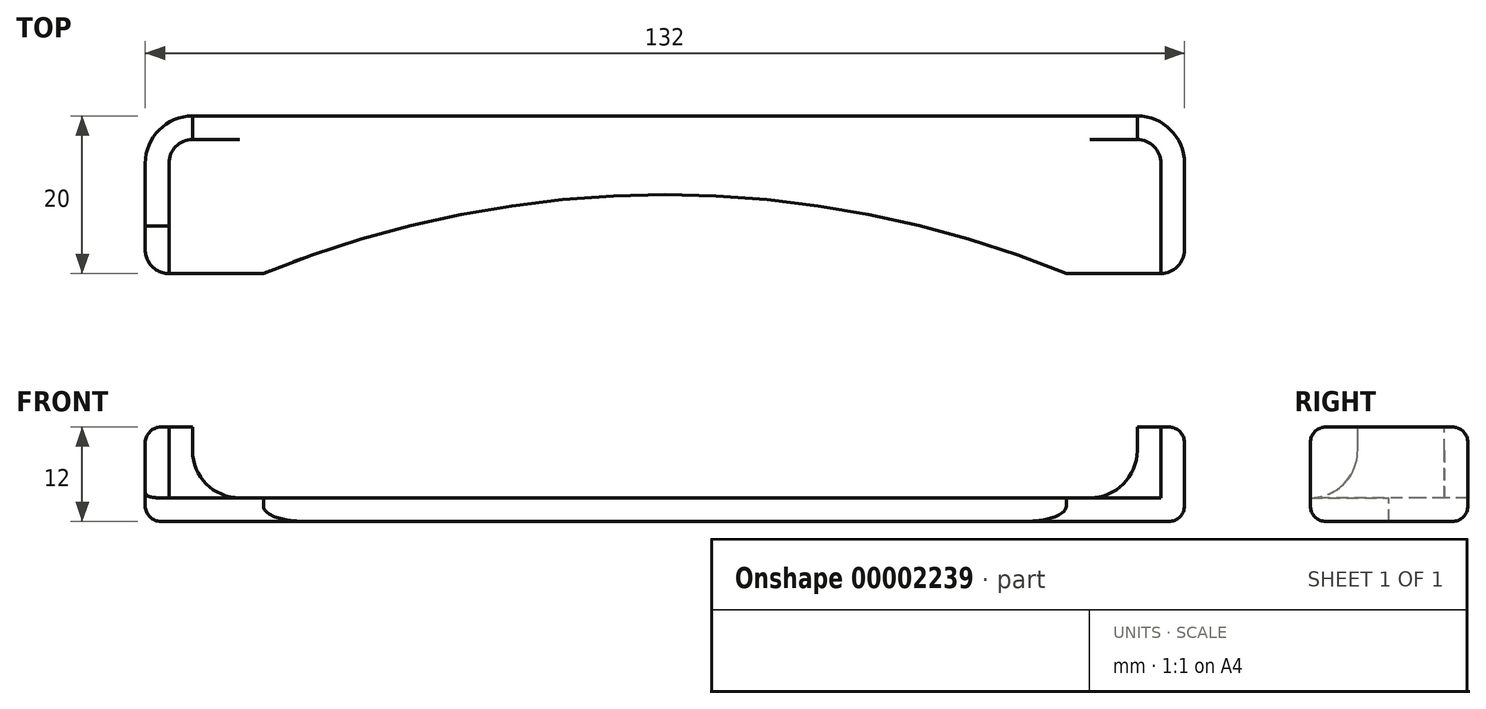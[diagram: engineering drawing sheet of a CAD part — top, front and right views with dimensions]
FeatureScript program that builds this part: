
annotation { "Feature Type Name" : "Feature", "Feature Type Description" : "" }
export const myFeature = defineFeature(function(context is Context, id is Id, definition is map)
    precondition{}
    {
        {
            var Q0;
            Q0=qCreatedBy(makeId("Top.planeOp"),FACE);
            var sketch = newSketch(context, id + "F0", { "sketchPlane" : qUnion([Q0])});
            skLineSegment(sketch, "E0.bottom", {"start": v(-60, 35) * mm, "end": v(60, 35) * mm});
            skLineSegment(sketch, "E0.top", {"start": v(-63, 15) * mm, "end": v(63, 15) * mm});
            skLineSegment(sketch, "E0.left", {"start": v(-66, 29) * mm, "end": v(-66, 18) * mm});
            skLineSegment(sketch, "E0.right", {"start": v(66, 29) * mm, "end": v(66, 18) * mm});
            skPoint(sketch, "E1.visualSharp", {"position": v(-66, 35) * mm});
            skArc(sketch, "E1.filletArc", {"start": v(-60, 35) * mm, "mid": v(-64.24, 33.24) * mm, "end": v(-66, 29) * mm});
            skPoint(sketch, "E2.visualSharp", {"position": v(66, 35) * mm});
            skArc(sketch, "E2.filletArc", {"start": v(66, 29) * mm, "mid": v(64.24, 33.24) * mm, "end": v(60, 35) * mm});
            skPoint(sketch, "E3.visualSharp", {"position": v(-66, 15) * mm});
            skArc(sketch, "E3.filletArc", {"start": v(-66, 18) * mm, "mid": v(-65.12, 15.88) * mm, "end": v(-63, 15) * mm});
            skPoint(sketch, "E4.visualSharp", {"position": v(66, 15) * mm});
            skArc(sketch, "E4.filletArc", {"start": v(63, 15) * mm, "mid": v(65.12, 15.88) * mm, "end": v(66, 18) * mm});
            skPoint(sketch, "E5", {"position": v(0, 15) * mm});
            skSolve(sketch);
        }
        {
            var Q0;
            Q0=makeQuery(id+"F0.imprint","IMPRINT",FACE,{"disambiguationData":[TD([[makeQuery(id+"F0.imprint","IMPRINT",EDGE,{"derivedFrom":sQuery(id+"F0.wireOp",EDGE,"E0.bottom")}),-1.0]])]});
            extrude(context, id + "F1", {"entities" : qUnion([Q0]), "depth" : 12 * mm});
        }
        {
            var Q0;
            Q0=makeQuery(id+"F1.opExtrude","CAP_FACE",FACE,{"disambiguationData":[OSD([sQuery(id+"F0.wireOp",EDGE,"E0.bottom"),sQuery(id+"F0.wireOp",EDGE,"E0.top"),sQuery(id+"F0.wireOp",EDGE,"E0.left"),sQuery(id+"F0.wireOp",EDGE,"E0.right"),sQuery(id+"F0.wireOp",EDGE,"E1.filletArc"),sQuery(id+"F0.wireOp",EDGE,"E2.filletArc"),sQuery(id+"F0.wireOp",EDGE,"E3.filletArc"),sQuery(id+"F0.wireOp",EDGE,"E4.filletArc")])],"isStart":false});
            var sketch = newSketch(context, id + "F2", { "sketchPlane" : qUnion([Q0])});
            skArc(sketch, "E6.1", {"start": v(63, 29) * mm, "mid": v(62.12, 31.12) * mm, "end": v(60, 32) * mm});
            skLineSegment(sketch, "E6.2", {"start": v(-60, 32) * mm, "end": v(60, 32) * mm});
            skArc(sketch, "E6.3", {"start": v(-60, 32) * mm, "mid": v(-62.12, 31.12) * mm, "end": v(-63, 29) * mm});
            skLineSegment(sketch, "E7", {"start": v(-63, 29) * mm, "end": v(-63, 15) * mm});
            skLineSegment(sketch, "E8", {"start": v(-63, 15) * mm, "end": v(63, 15) * mm});
            skLineSegment(sketch, "E9", {"start": v(63, 15) * mm, "end": v(63, 29) * mm});
            skSolve(sketch);
        }
        {
            var Q0;
            Q0=makeQuery(id+"F1.opExtrude","CAP_FACE",FACE,{"disambiguationData":[OSD([sQuery(id+"F0.wireOp",EDGE,"E0.bottom"),sQuery(id+"F0.wireOp",EDGE,"E0.top"),sQuery(id+"F0.wireOp",EDGE,"E0.left"),sQuery(id+"F0.wireOp",EDGE,"E0.right"),sQuery(id+"F0.wireOp",EDGE,"E1.filletArc"),sQuery(id+"F0.wireOp",EDGE,"E2.filletArc"),sQuery(id+"F0.wireOp",EDGE,"E3.filletArc"),sQuery(id+"F0.wireOp",EDGE,"E4.filletArc")])],"isStart":false});
            var Q1;
            Q1=makeQuery(id+"F1.opExtrude","CAP_FACE",FACE,{"disambiguationData":[OSD([sQuery(id+"F0.wireOp",EDGE,"E0.bottom"),sQuery(id+"F0.wireOp",EDGE,"E0.top"),sQuery(id+"F0.wireOp",EDGE,"E0.left"),sQuery(id+"F0.wireOp",EDGE,"E0.right"),sQuery(id+"F0.wireOp",EDGE,"E1.filletArc"),sQuery(id+"F0.wireOp",EDGE,"E2.filletArc"),sQuery(id+"F0.wireOp",EDGE,"E3.filletArc"),sQuery(id+"F0.wireOp",EDGE,"E4.filletArc")])],"isStart":true});
            fillet(context, id + "F3", {"entities" : qUnion([Q0, Q1]), "radius" : 2 * mm, "allowEdgeOverflow" : false});
        }
        {
            var Q0;
            Q0=makeQuery(id+"F2.imprint","IMPRINT",FACE,{"disambiguationData":[TD([[makeQuery(id+"F2.imprint","IMPRINT",EDGE,{"derivedFrom":sQuery(id+"F2.wireOp",EDGE,"001a4620-0fa9-427e-a59e-a394cfe2f85a.bottom")}),-1.0]])]});
            var Q1;
            Q1=makeQuery(id+"F2.imprint","IMPRINT",FACE,{"disambiguationData":[TD([[makeQuery(id+"F2.imprint","IMPRINT",EDGE,{"derivedFrom":sQuery(id+"F2.wireOp",EDGE,"E6.1")}),1.0]])]});
            extrude(context, id + "F4", {"entities" : qUnion([Q0, Q1]), "operationType" : NewBodyOperationType.REMOVE, "oppositeDirection" : true, "depth" : 9 * mm});
        }
        {
            var Q0;
            Q0=makeQuery(id+"F4.boolean.opBoolean","COPY",FACE,{"derivedFrom":makeQuery(id+"F4.opExtrude","CAP_FACE",FACE,{"disambiguationData":[OSD([sQuery(id+"F2.wireOp",EDGE,"E6.1"),sQuery(id+"F2.wireOp",EDGE,"E6.2"),sQuery(id+"F2.wireOp",EDGE,"E6.3"),sQuery(id+"F2.wireOp",EDGE,"E7"),sQuery(id+"F2.wireOp",EDGE,"E8"),sQuery(id+"F2.wireOp",EDGE,"E9")])],"isStart":false})});
            var sketch = newSketch(context, id + "F5", { "sketchPlane" : qUnion([Q0])});
            skArc(sketch, "E10", {"start": v(51, 15) * mm, "mid": v(0, 25) * mm, "end": v(-51, 15) * mm});
            skLineSegment(sketch, "E11", {"start": v(-51, 15) * mm, "end": v(51, 15) * mm});
            skLineSegment(sketch, "E12", {"start": v(0, 15) * mm, "end": v(0, -110.05) * mm, "construction": true});
            skSolve(sketch);
        }
        {
            var Q0;
            Q0=makeQuery(id+"F5.imprint","IMPRINT",FACE,{"disambiguationData":[TD([[makeQuery(id+"F5.imprint","IMPRINT",EDGE,{"derivedFrom":sQuery(id+"F5.wireOp",EDGE,"E10")}),1.0]])]});
            extrude(context, id + "F6", {"entities" : qUnion([Q0]), "operationType" : NewBodyOperationType.REMOVE, "endBound" : BoundingType.THROUGH_ALL, "oppositeDirection" : true, "depth" : 25 * mm});
        }
        {
            var Q0;
            Q0=makeQuery(id+"F4.boolean.opBoolean","COPY",FACE,{"derivedFrom":makeQuery(id+"F4.opExtrude","SWEPT_FACE",FACE,{"disambiguationData":[OSD([sQuery(id+"F2.wireOp",EDGE,"E6.2")])]})});
            var sketch = newSketch(context, id + "F7", { "sketchPlane" : qUnion([Q0])});
            skLineSegment(sketch, "E13", {"start": v(-60, 12) * mm, "end": v(-60, 9) * mm});
            skArc(sketch, "E14", {"start": v(-60, 9) * mm, "mid": v(-58.24, 4.76) * mm, "end": v(-54, 3) * mm});
            skLineSegment(sketch, "E15", {"start": v(-54, 3) * mm, "end": v(0, 3) * mm});
            skLineSegment(sketch, "E16", {"start": v(0, 3) * mm, "end": v(0, 12) * mm, "construction": true});
            skLineSegment(sketch, "E17", {"start": v(0, 12) * mm, "end": v(-60, 12) * mm});
            skLineSegment(sketch, "E18.0.MirrorCS", {"start": v(0, 12) * mm, "end": v(60, 12) * mm});
            skLineSegment(sketch, "E19.0.MirrorCS", {"start": v(60, 12) * mm, "end": v(60, 9) * mm});
            skArc(sketch, "E20.0.MirrorCS", {"start": v(60, 9) * mm, "mid": v(58.24, 4.76) * mm, "end": v(54, 3) * mm});
            skLineSegment(sketch, "E21.0.MirrorCS", {"start": v(54, 3) * mm, "end": v(0, 3) * mm});
            skSolve(sketch);
        }
        {
            var Q0;
            Q0=makeQuery(id+"F7.imprint","IMPRINT",FACE,{"disambiguationData":[TD([[makeQuery(id+"F7.imprint","IMPRINT",EDGE,{"derivedFrom":sQuery(id+"F7.wireOp",EDGE,"E13")}),-1.0]])]});
            extrude(context, id + "F8", {"entities" : qUnion([Q0]), "operationType" : NewBodyOperationType.REMOVE, "endBound" : BoundingType.THROUGH_ALL, "oppositeDirection" : true, "depth" : 25 * mm});
        }
        {
            var Q0;
            Q0=makeQuery(id+"F4.boolean.opBoolean","COPY",FACE,{"derivedFrom":makeQuery(id+"F4.opExtrude","SWEPT_FACE",FACE,{"disambiguationData":[OSD([sQuery(id+"F2.wireOp",EDGE,"E7")])]})});
            var sketch = newSketch(context, id + "F9", { "sketchPlane" : qUnion([Q0])});
            skArc(sketch, "E22", {"start": v(15, 3) * mm, "mid": v(19.24, 4.76) * mm, "end": v(21, 9) * mm});
            skLineSegment(sketch, "E23", {"start": v(21, 9) * mm, "end": v(21, 12) * mm});
            skSolve(sketch);
        }
        {
            var Q0;
            Q0=makeQuery(id+"F9.imprint","IMPRINT",FACE,{"disambiguationData":[TD([[makeQuery(id+"F9.imprint","IMPRINT",EDGE,{"derivedFrom":sQuery(id+"F9.wireOp",EDGE,"E22")}),1.0]])]});
            extrude(context, id + "F10", {"entities" : qUnion([Q0]), "operationType" : NewBodyOperationType.REMOVE, "endBound" : BoundingType.THROUGH_ALL, "oppositeDirection" : true, "depth" : 200 * mm});
        }
    });
